# Revit family: Receptor-Sani-Flor_16_Inch_Square_Top-Zurn-Z1926-12_Inch_Sump
name_source: partatom
category: Plumbing Fixtures
units: mm (PartAtom-declared; Revit-internal decimal feet)

## family parameters
Always vertical = Yes
Cut with Voids When Loaded = No
Maintain Annotation Orientation = No
OmniClass Number = 23.70.50.21.24.14
OmniClass Title = Deck Waste Water Drains
Part Type = Normal
Room Calculation Point = No
Round Connector Dimension = Use Radius
Shared = No
Work Plane-Based = No

## types (18) — shared parameters
Approx. Weight (Lbs) = 150 "
Assembly Code = D2030300
CW Connection = No
Default Elevation = 25 "
Description = 16 X 16 [406 X 406] A.R.C. SANI-FLOR RECEPTOR 12 [305] SUMP DEPTH
HW Connection = No
Main Material = Cast Iron- Zurn- White A.R.E Coated- Interior
Manufacturer = Zurn Water, LLC
Manufacurer Brand = Zurn
Model = Z1926
Modified Date = 09/02/2025
Product Documentation Link = https://files.zurn.com
Product Page URL = https://www.zurn.com
Product data url = https://bimobject.com
Sump Depth = 12 "
URL = www.zurn.com
Vent Connection = No
WFU = 1
Waste Connection = Yes
Width = 13.25 "
zero-valued in all types: CWFU, HWFU

## per-type parameters (varying)
| type | Body Height_E | Frame and Grate | Outlet Connector | Pipe Size Radius_A (Actual) | Pipe Size Radius_A (Nominal) | Sani-Flor Receptor | Type Comments |
| Z1926-2NH Outlet | 15 " | Cast Iron- Zurn- White A.R.E Coated- Interior | 1 " | 1.188 " | 1 " | 16 " | Z1926-2 Inch -No-Hub Outlet |
| Z1926-2NL Outlet | 14.25 " | Cast Iron- Zurn- White A.R.E Coated- Interior | 1 " | 1.188 " | 1 " | 16 " | Z1926-2 Inch -Neo-Loc Outlet |
| Z1926-3IC Outlet | 15 " | Cast Iron- Zurn- White A.R.E Coated- Interior | 1.5 " | 1.75 " | 1.5 " | 16 " | Z1926-3 Inch -Inside Caulk Outlet |
| Z1926-3NH Outlet | 15 " | Cast Iron- Zurn- White A.R.E Coated- Interior | 1.5 " | 1.75 " | 1.5 " | 16 " | Z1926-3 Inch -No-Hub Outlet |
| Z1926-3NL Outlet | 14.25 " | Cast Iron- Zurn- White A.R.E Coated- Interior | 1.5 " | 1.75 " | 1.5 " | 16 " | Z1926-3 Inch -Neo-Loc Outlet |
| Z1926-4IC Outlet | 15 " | Cast Iron- Zurn- White A.R.E Coated- Interior | 2 " | 2.25 " | 2 " | 16 " | Z1926-4 Inch -Inside Caulk Outlet |
| Z1926-4NH Outlet | 15 " | Cast Iron- Zurn- White A.R.E Coated- Interior | 2 " | 2.25 " | 2 " | 16 " | Z1926-4 Inch -No-Hub Outlet |
| Z1926-4NL Outlet | 14.25 " | Cast Iron- Zurn- White A.R.E Coated- Interior | 2 " | 2.25 " | 2 " | 16 " | Z1926-4 Inch -Neo-Loc Outlet |
| Z1926-6IC Outlet | 15 " | Cast Iron- Zurn- White A.R.E Coated- Interior | 3 " | 3.313 " | 3 " | 16 " | Z1926-6 Inch -Inside Caulk Outlet |
| ZN1926-2NH Outlet | 15.188 " | Bronze - Zurn - Polished Nickel | 1 " | 1.188 " | 1 " | 16.75 " | ZN1926-2 Inch -No-Hub Outlet |
| ZN1926-2NL Outlet | 14.438 " | Bronze - Zurn - Polished Nickel | 1 " | 1.188 " | 1 " | 16.75 " | ZN1926-2 Inch -Neo-Loc Outlet |
| ZN1926-3IC Outlet | 15.188 " | Bronze - Zurn - Polished Nickel | 1.5 " | 1.75 " | 1.5 " | 16.75 " | Z1926-3 Inch -Inside Caulk Outlet |
| ZN1926-3NH Outlet | 15.188 " | Bronze - Zurn - Polished Nickel | 1.5 " | 1.75 " | 1.5 " | 16.75 " | ZN1926-3 Inch -No-Hub Outlet |
| ZN1926-3NL Outlet | 14.438 " | Bronze - Zurn - Polished Nickel | 1.5 " | 1.75 " | 1.5 " | 16.75 " | ZN1926-3 Inch -Neo-Loc Outlet |
| ZN1926-4IC Outlet | 15.188 " | Bronze - Zurn - Polished Nickel | 2 " | 2.25 " | 2 " | 16.75 " | ZN1926-4 Inch -Inside Caulk Outlet |
| ZN1926-4NH Outlet | 15.188 " | Bronze - Zurn - Polished Nickel | 2 " | 2.25 " | 2 " | 16.75 " | ZN1926-4 Inch -No-Hub Outlet |
| ZN1926-4NL Outlet | 14.438 " | Bronze - Zurn - Polished Nickel | 2 " | 2.25 " | 2 " | 16.75 " | ZN1926-4 Inch -Neo-Loc Outlet |
| ZN1926-6IC Outlet | 15.188 " | Bronze - Zurn - Polished Nickel | 3 " | 3.313 " | 3 " | 16.75 " | ZN1926-6 Inch -Inside Caulk Outlet |

## geometry (parser evidence)
native form markers: Sweep x5
no freeform markers — native parametric forms only
